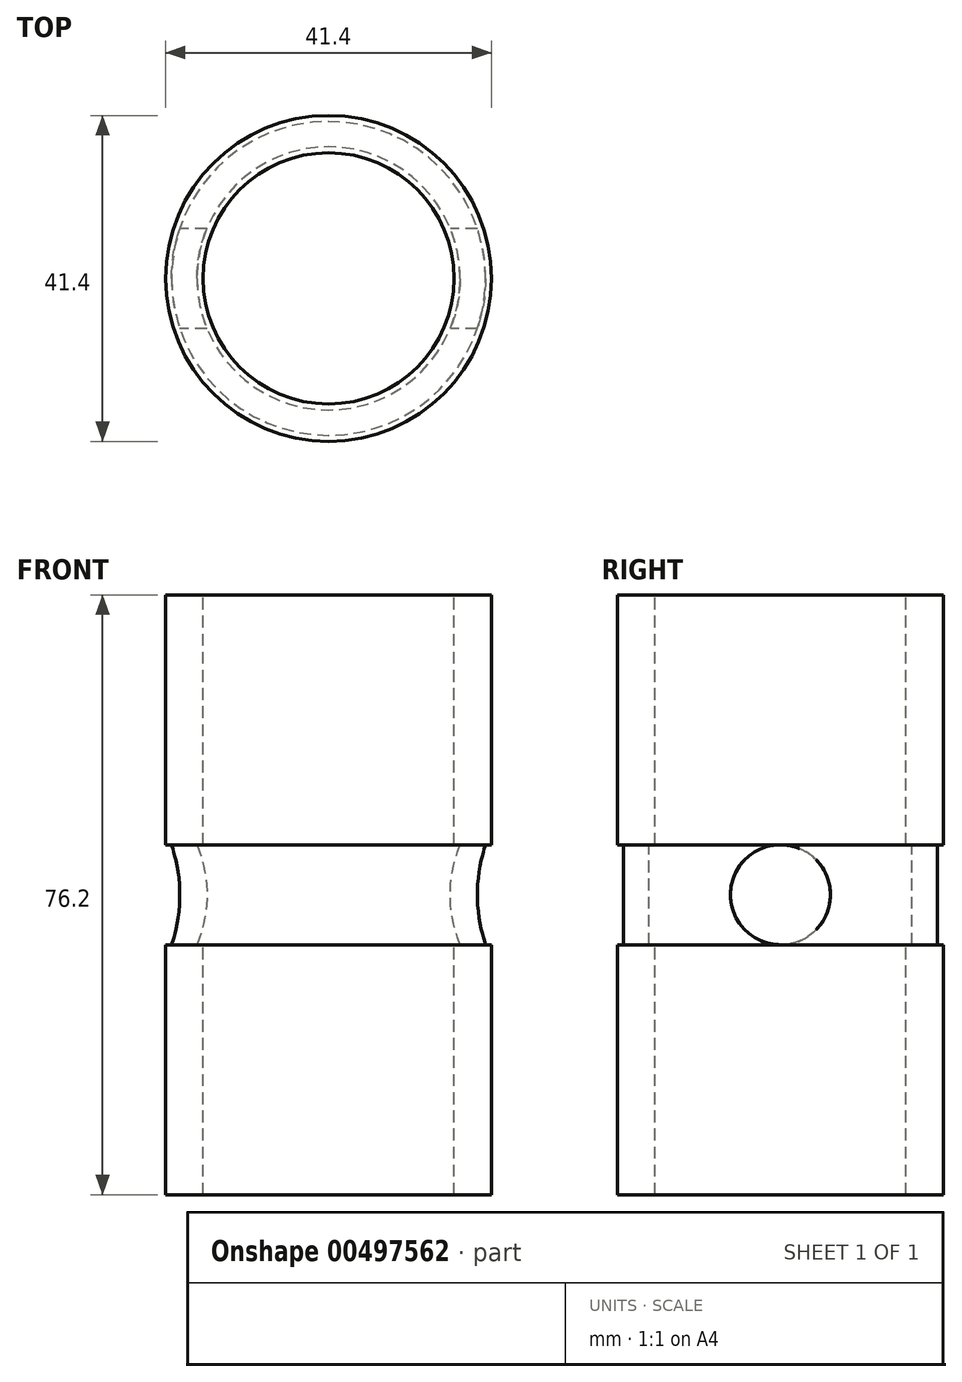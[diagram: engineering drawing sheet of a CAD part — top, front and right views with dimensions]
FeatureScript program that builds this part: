
annotation { "Feature Type Name" : "Feature", "Feature Type Description" : "" }
export const myFeature = defineFeature(function(context is Context, id is Id, definition is map)
    precondition{}
    {
        {
            var Q0;
            Q0=qCreatedBy(makeId("Front.planeOp"),FACE);
            var sketch = newSketch(context, id + "F0", { "sketchPlane" : qUnion([Q0])});
            skLineSegment(sketch, "E0", {"start": v(0, 0) * mm, "end": v(0, -31.75) * mm});
            skLineSegment(sketch, "E1", {"start": v(0, -31.75) * mm, "end": v(0.76, -31.75) * mm});
            skLineSegment(sketch, "E2", {"start": v(0.76, -31.75) * mm, "end": v(0.76, -44.45) * mm});
            skLineSegment(sketch, "E3", {"start": v(0.76, -44.45) * mm, "end": v(0, -44.45) * mm});
            skLineSegment(sketch, "E4", {"start": v(0, -44.45) * mm, "end": v(0, -76.2) * mm});
            skLineSegment(sketch, "E5", {"start": v(0, -76.2) * mm, "end": v(4.75, -76.2) * mm});
            skLineSegment(sketch, "E6", {"start": v(4.75, -76.2) * mm, "end": v(4.75, -44.45) * mm});
            skLineSegment(sketch, "E7", {"start": v(4.75, -44.45) * mm, "end": v(3.99, -44.45) * mm});
            skLineSegment(sketch, "E8", {"start": v(3.99, -44.45) * mm, "end": v(3.99, -31.75) * mm});
            skLineSegment(sketch, "E9", {"start": v(3.99, -31.75) * mm, "end": v(4.75, -31.75) * mm});
            skLineSegment(sketch, "E10", {"start": v(4.75, -31.75) * mm, "end": v(4.75, 0) * mm});
            skLineSegment(sketch, "E11", {"start": v(4.75, 0) * mm, "end": v(0, 0) * mm});
            skLineSegment(sketch, "E12", {"start": v(0, 0) * mm, "end": v(20.7, 0) * mm, "construction": true});
            skLineSegment(sketch, "E13", {"start": v(20.7, 0) * mm, "end": v(20.7, -76.2) * mm, "construction": true});
            skSolve(sketch);
        }
        {
            var Q0;
            Q0=makeQuery(id+"F0.imprint","IMPRINT",FACE,{"disambiguationData":[TD([[makeQuery(id+"F0.imprint","IMPRINT",EDGE,{"derivedFrom":sQuery(id+"F0.wireOp",EDGE,"E0")}),1.0]])]});
            var Q1;
            Q1=sQuery(id+"F0.wireOp",EDGE,"E13");
            revolve(context, id + "F1", {"entities" : qUnion([Q0]), "axis" : qUnion([Q1]), "revolveType" : RevolveType.FULL});
        }
        {
            var Q0;
            Q0=qCreatedBy(makeId("Right.planeOp"),FACE);
            var sketch = newSketch(context, id + "F2", { "sketchPlane" : qUnion([Q0])});
            skLineSegment(sketch, "E14", {"start": v(0, 0) * mm, "end": v(0, -38.1) * mm, "construction": true});
            skSolve(sketch);
        }
        {
            var Q0;
            Q0=sQuery(id+"F2.wireOp",VERTEX,"E14.end");
            var Q1;
            Q1=makeQuery(id+"F1.opRevolve","SWEPT_BODY",BODY,{"disambiguationData":[OSD([sQuery(id+"F0.wireOp",EDGE,"E0"),sQuery(id+"F0.wireOp",EDGE,"E1"),sQuery(id+"F0.wireOp",EDGE,"E2"),sQuery(id+"F0.wireOp",EDGE,"E3"),sQuery(id+"F0.wireOp",EDGE,"E4"),sQuery(id+"F0.wireOp",EDGE,"E5"),sQuery(id+"F0.wireOp",EDGE,"E6"),sQuery(id+"F0.wireOp",EDGE,"E7"),sQuery(id+"F0.wireOp",EDGE,"E8"),sQuery(id+"F0.wireOp",EDGE,"E9"),sQuery(id+"F0.wireOp",EDGE,"E10"),sQuery(id+"F0.wireOp",EDGE,"E11")])]});
            hole(context, id + "F3", {"style" : HoleStyle.SIMPLE, "endStyle" : HoleEndStyle.THROUGH, "oppositeDirection" : true, "holeDiameter" : 12.7 * mm, "isTappedThrough" : true, "tappedDepth" : 12.7 * mm, "tapClearance" : 3, "locations" : qUnion([Q0]), "scope" : qUnion([Q1])});
        }
    });
